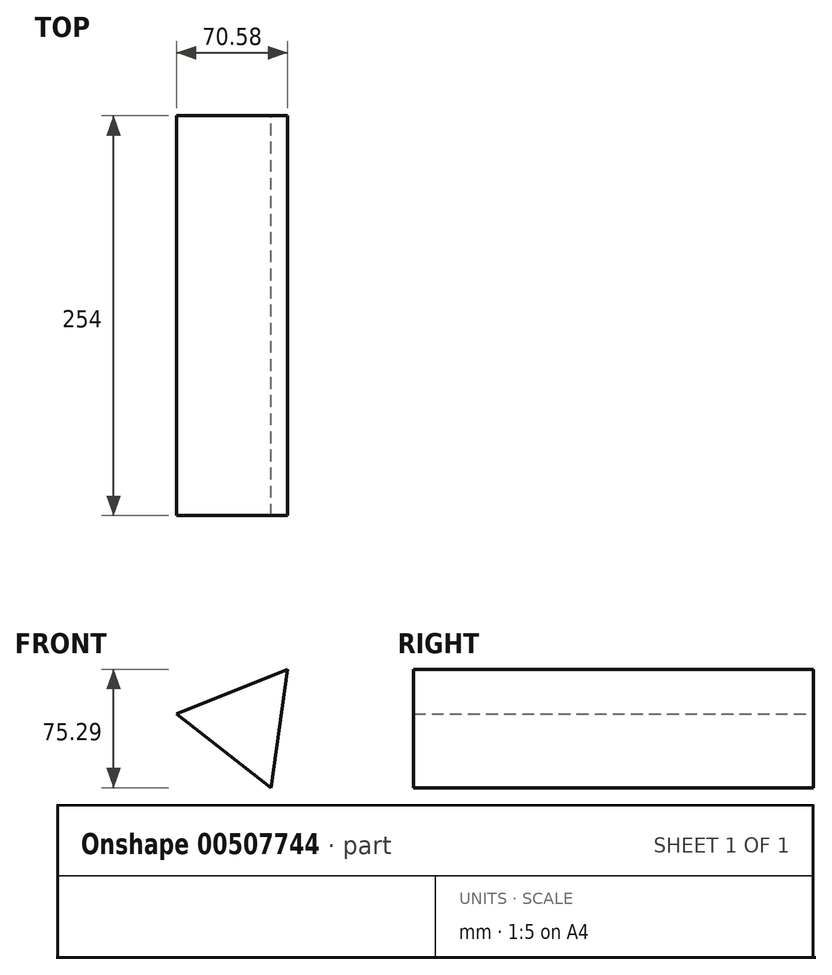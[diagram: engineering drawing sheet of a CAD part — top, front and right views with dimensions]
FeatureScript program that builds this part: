
annotation { "Feature Type Name" : "Feature", "Feature Type Description" : "" }
export const myFeature = defineFeature(function(context is Context, id is Id, definition is map)
    precondition{}
    {
        {
            var Q0;
            Q0=qCreatedBy(makeId("Front.planeOp"),FACE);
            var sketch = newSketch(context, id + "F0", { "sketchPlane" : qUnion([Q0])});
            skCircle(sketch, "E0.cCircle", {"center": v(0, 0) * mm, "radius": 43.9 * mm, "construction": true});
            skLineSegment(sketch, "E0.0", {"start": v(27.1, 34.54) * mm, "end": v(16.36, -40.75) * mm});
            skLineSegment(sketch, "E0.1", {"start": v(16.36, -40.75) * mm, "end": v(-43.47, 6.2) * mm});
            skLineSegment(sketch, "E0.2", {"start": v(-43.47, 6.2) * mm, "end": v(27.1, 34.54) * mm});
            skSolve(sketch);
        }
        {
            var Q0;
            Q0=makeQuery(id+"F0.imprint","IMPRINT",FACE,{"disambiguationData":[TD([[makeQuery(id+"F0.imprint","IMPRINT",EDGE,{"derivedFrom":sQuery(id+"F0.wireOp",EDGE,"E0.0")}),-1.0]])]});
            extrude(context, id + "F1", {"entities" : qUnion([Q0]), "depth" : 254 * mm});
        }
    });
